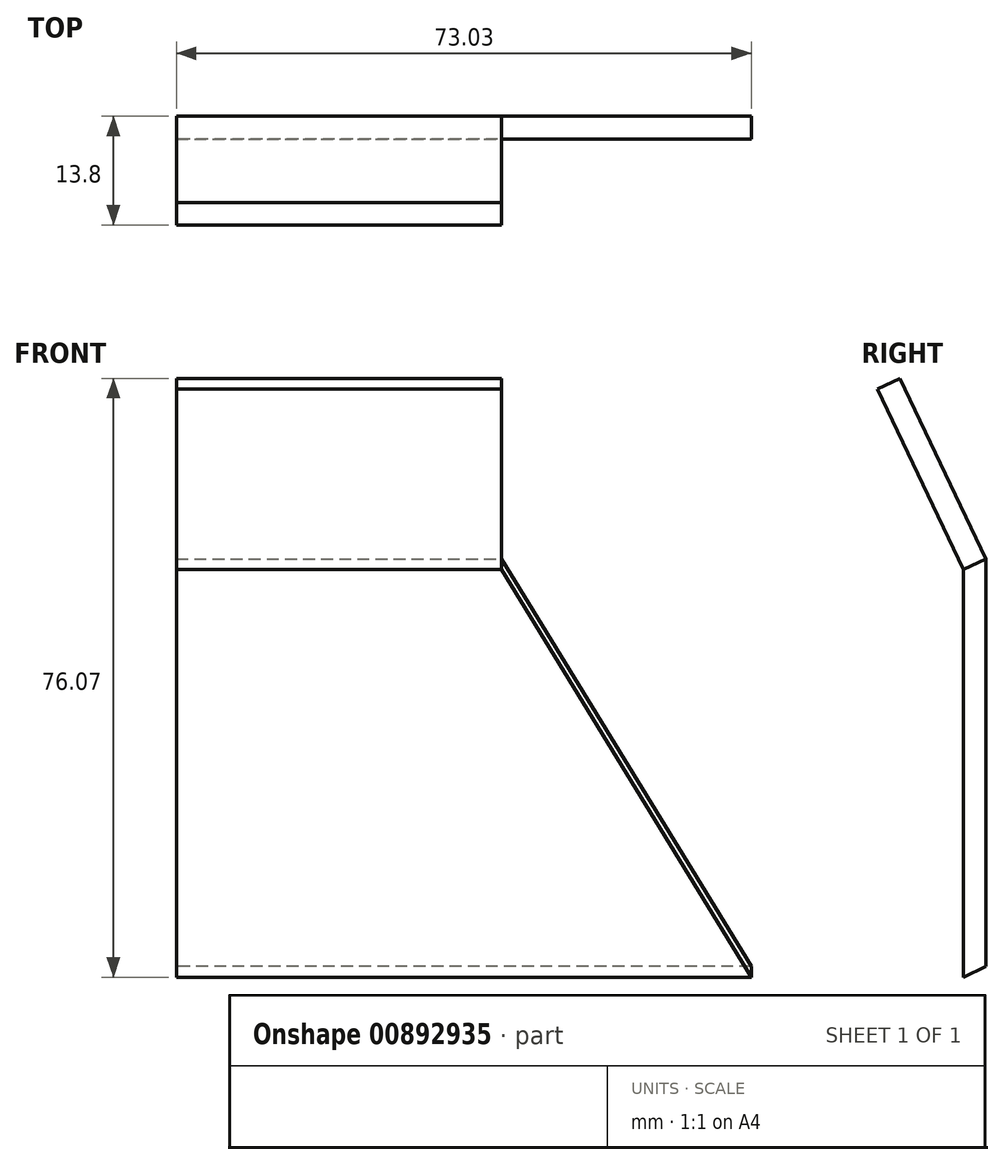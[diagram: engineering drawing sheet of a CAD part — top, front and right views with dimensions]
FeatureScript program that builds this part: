
annotation { "Feature Type Name" : "Feature", "Feature Type Description" : "" }
export const myFeature = defineFeature(function(context is Context, id is Id, definition is map)
    precondition{}
    {
        {
            var Q0;
            Q0=qCreatedBy(makeId("Front.planeOp"),FACE);
            var sketch = newSketch(context, id + "F0", { "sketchPlane" : qUnion([Q0])});
            skPoint(sketch, "E0.0", {"position": v(0, 51.78) * mm});
            skLineSegment(sketch, "E1", {"start": v(0, 51.78) * mm, "end": v(41.28, 51.78) * mm});
            skLineSegment(sketch, "E2", {"start": v(41.28, 51.78) * mm, "end": v(73.03, 0) * mm});
            skPoint(sketch, "E3.0", {"position": v(0, 0) * mm});
            skLineSegment(sketch, "E4", {"start": v(73.02, 0) * mm, "end": v(0, 0) * mm});
            skLineSegment(sketch, "E5", {"start": v(0, 0) * mm, "end": v(0, 51.78) * mm});
            skSolve(sketch);
        }
        {
            var Q0;
            Q0=sQuery(id+"F0.wireOp",EDGE,"E1");
            cPlane(context, id + "F1", {"entities" : qUnion([Q0]), "cplaneType" : CPlaneType.LINE_ANGLE, "offset" : 25.4 * mm, "angle" : 154.5 * degree, "oppositeDirection" : true, "width" : 152.4 * mm, "height" : 152.4 * mm});
        }
        {
            var Q0;
            Q0=qCreatedBy(id+"F1.planeOp",FACE);
            var sketch = newSketch(context, id + "F2", { "sketchPlane" : qUnion([Q0])});
            skPoint(sketch, "E6.0", {"position": v(41.28, 46.74) * mm});
            skPoint(sketch, "E7.0", {"position": v(41.27, 72.14) * mm});
            skLineSegment(sketch, "E8", {"start": v(41.28, 46.74) * mm, "end": v(41.28, 72.14) * mm});
            skPoint(sketch, "E9.0", {"position": v(0, 46.74) * mm});
            skLineSegment(sketch, "E10", {"start": v(0, 72.14) * mm, "end": v(0, 46.74) * mm});
            skLineSegment(sketch, "E11", {"start": v(0, 46.74) * mm, "end": v(41.28, 46.74) * mm});
            skLineSegment(sketch, "E12", {"start": v(41.28, 72.14) * mm, "end": v(0, 72.14) * mm});
            skSolve(sketch);
        }
        {
            var Q0;
            Q0=makeQuery(id+"F2.imprint","IMPRINT",FACE,{"disambiguationData":[TD([[makeQuery(id+"F2.imprint","IMPRINT",EDGE,{"derivedFrom":sQuery(id+"F2.wireOp",EDGE,"E8")}),1.0]])]});
            var Q1;
            Q1=makeQuery(id+"F0.imprint","IMPRINT",FACE,{"disambiguationData":[TD([[makeQuery(id+"F0.imprint","IMPRINT",EDGE,{"derivedFrom":sQuery(id+"F0.wireOp",EDGE,"E1")}),-1.0]])]});
            extrude(context, id + "F3", {"entities" : qUnion([Q0, Q1]), "oppositeDirection" : true, "depth" : 3.17 * mm, "offsetDistance" : 25.4 * mm});
        }
    });
